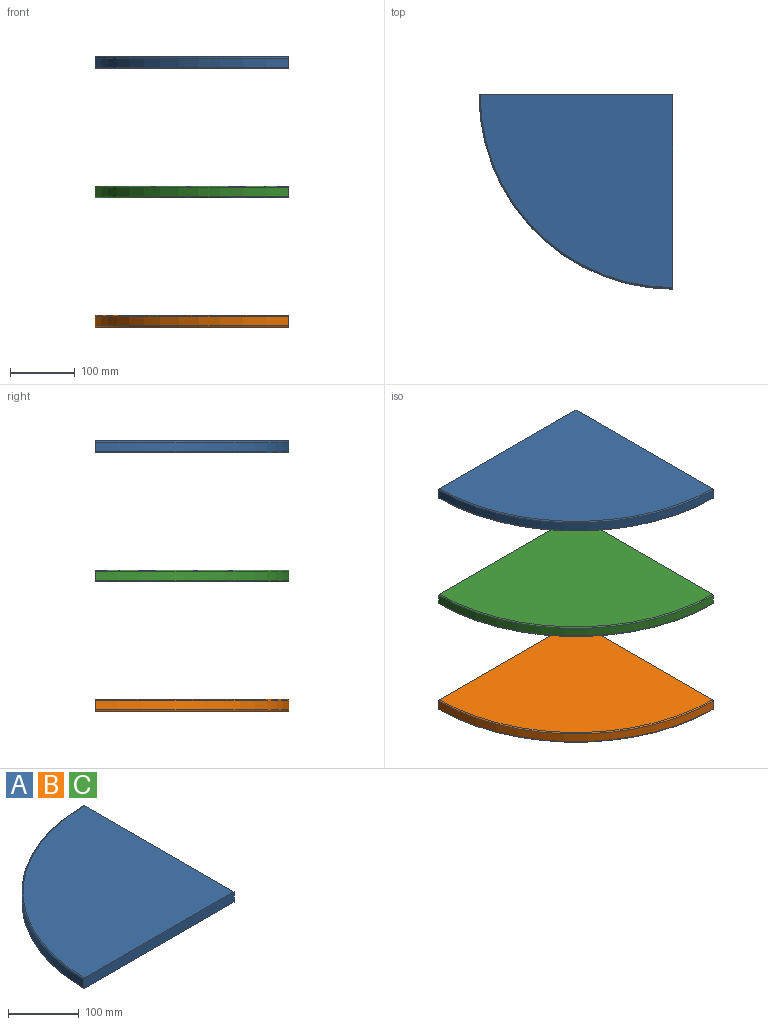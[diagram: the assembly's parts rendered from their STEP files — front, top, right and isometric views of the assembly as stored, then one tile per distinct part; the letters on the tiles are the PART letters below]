
ASSEMBLY  parts=3 mates=6
PART A: 7 faces, bbox 324.7x324.7x18 mm
  f0: cylinder r=300mm len=300mm, axis (0,0,-1), area 6785.8mm2, adj f1,f2,f5,f6
  f1: plane 300x18mm, normal (0,-1,0), area 5398.6mm2, adj f0,f2,f3,f4,f5,f6
  f2: plane 300x18mm, normal (1,0,0), area 5398.6mm2, adj f0,f1,f3,f4,f5,f6
  f3: plane 298.2x298.2mm, normal (0,0,1), area 69840.1mm2, adj f1,f2,f6
  f4: plane 298.2x298.2mm, normal (0,0,-1), area 69840.1mm2, adj f1,f2,f5
  f5: torus R=298.2mm, axis (0,0,1), area 1329.5mm2, adj f0,f1,f2,f4
  f6: torus R=298.2mm, axis (0,0,1), area 1329.5mm2, adj f0,f1,f2,f3
PART B: same geometry as A
PART C: same geometry as A
PLACE A rot(axis=(0,0,1),90deg) t=(-132.64,127.22,170.01)mm
PLACE B rot(axis=(0,0,1),90deg) t=(-132.64,127.22,-229.99)mm
PLACE C rot(axis=(0,0,1),90deg) t=(-132.64,127.22,-29.99)mm
MATE parallel C.f3 <-> B.f3  axis (0,0,1) through (-259.2,0.66,-11.99)mm
MATE planar C.f2 <-> A.f2  axis (0,1,0) through (-282.6,127.22,-20.99)mm
MATE parallel C.f3 <-> A.f3  axis (0,0,1) through (-259.2,0.66,-11.99)mm
MATE planar B.f1 <-> C.f1  axis (1,0,0) through (-132.64,-22.74,-220.99)mm
MATE planar C.f2 <-> B.f2  axis (0,1,0) through (-282.6,127.22,-20.99)mm
MATE planar A.f1 <-> C.f1  axis (1,0,0) through (-132.64,-22.74,179.01)mm
